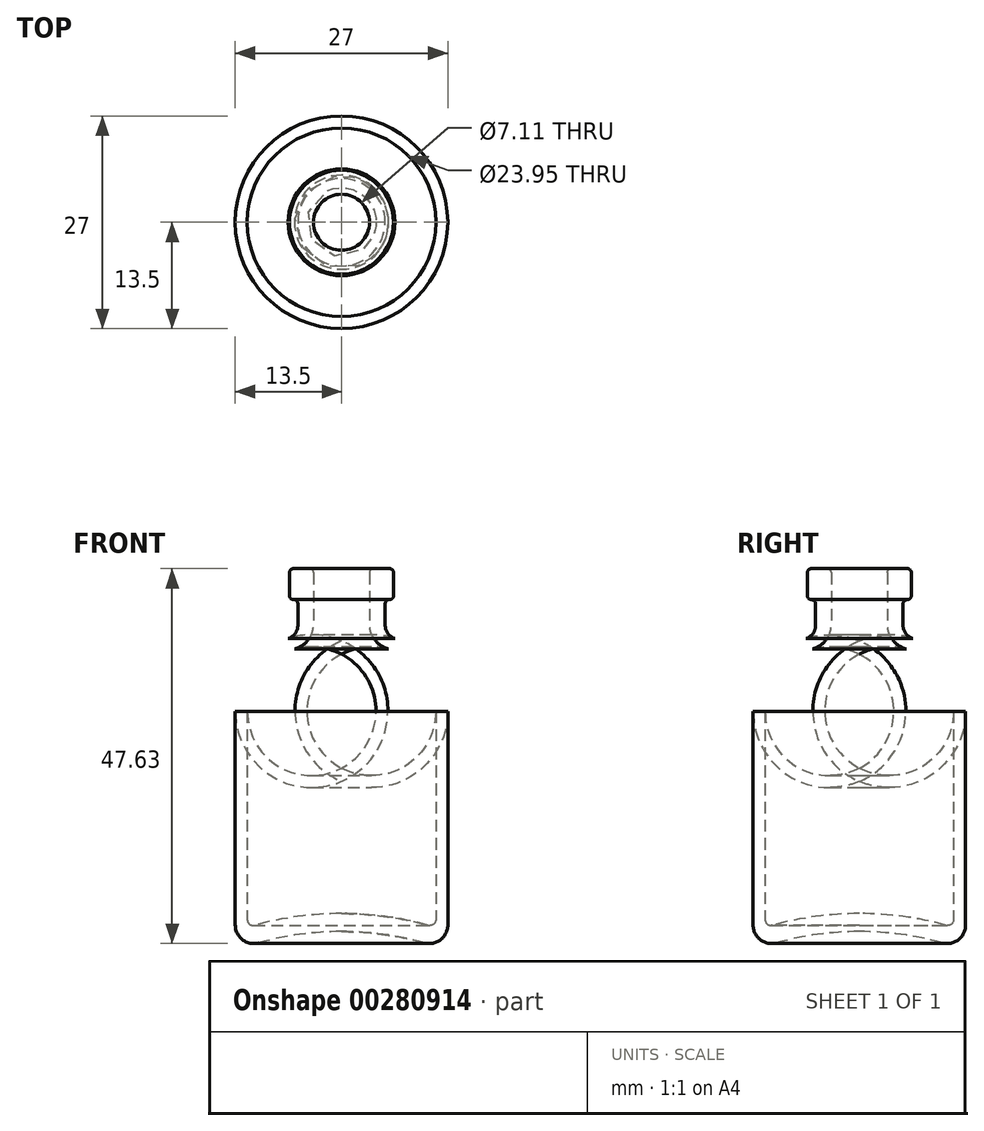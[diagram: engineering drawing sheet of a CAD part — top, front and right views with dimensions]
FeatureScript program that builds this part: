
annotation { "Feature Type Name" : "Feature", "Feature Type Description" : "" }
export const myFeature = defineFeature(function(context is Context, id is Id, definition is map)
    precondition{}
    {
        {
            var Q0;
            Q0=qCreatedBy(makeId("Front.planeOp"),FACE);
            var sketch = newSketch(context, id + "F0", { "sketchPlane" : qUnion([Q0])});
            skLineSegment(sketch, "E0", {"start": v(13.5, 29.51) * mm, "end": v(13.5, 2.36) * mm});
            skLineSegment(sketch, "E1", {"start": v(0, 0) * mm, "end": v(28.43, 0) * mm, "construction": true});
            skArc(sketch, "E2", {"start": v(10.5, 0.09) * mm, "mid": v(12.57, 0.48) * mm, "end": v(13.5, 2.36) * mm});
            skLineSegment(sketch, "E3", {"start": v(0.17, 1.52) * mm, "end": v(-0.17, 1.52) * mm, "construction": true});
            skLineSegment(sketch, "E4", {"start": v(0, 0) * mm, "end": v(0, 24.8) * mm, "construction": true});
            skPoint(sketch, "E4.endSnap0", {"position": v(0, 1.52) * mm});
            skArc(sketch, "E5", {"start": v(10.5, 0.09) * mm, "mid": v(5.3, 1.16) * mm, "end": v(0, 1.52) * mm});
            skArc(sketch, "E6", {"start": v(13.5, 29.51) * mm, "mid": v(11.64, 35.22) * mm, "end": v(6.78, 38.75) * mm});
            skLineSegment(sketch, "E7", {"start": v(5.55, 40.44) * mm, "end": v(5.55, 43.69) * mm});
            skLineSegment(sketch, "E8", {"start": v(5.55, 43.69) * mm, "end": v(6.6, 43.69) * mm});
            skLineSegment(sketch, "E9", {"start": v(6.6, 43.69) * mm, "end": v(6.6, 47.63) * mm});
            skLineSegment(sketch, "E10", {"start": v(6.6, 47.63) * mm, "end": v(3.56, 47.63) * mm});
            skLineSegment(sketch, "E11", {"start": v(3.56, 47.63) * mm, "end": v(3.56, 40.58) * mm});
            skPoint(sketch, "E12.newPointA", {"position": v(5.55, 40) * mm});
            skArc(sketch, "E12.filletArc", {"start": v(5.55, 40.44) * mm, "mid": v(5.9, 39.4) * mm, "end": v(6.78, 38.75) * mm});
            skArc(sketch, "E13", {"start": v(11.98, 29.51) * mm, "mid": v(10.3, 34.47) * mm, "end": v(5.98, 37.4) * mm});
            skArc(sketch, "E14", {"start": v(3.56, 40.58) * mm, "mid": v(4.23, 38.58) * mm, "end": v(5.98, 37.4) * mm});
            skArc(sketch, "E15.0", {"start": v(11.01, 2.32) * mm, "mid": v(5.56, 3.44) * mm, "end": v(0, 3.8) * mm});
            skLineSegment(sketch, "E16.0", {"start": v(11.98, 29.51) * mm, "end": v(11.98, 3.05) * mm});
            skArc(sketch, "E17.filletArc", {"start": v(11.01, 2.32) * mm, "mid": v(11.68, 2.45) * mm, "end": v(11.98, 3.05) * mm});
            skLineSegment(sketch, "E18", {"start": v(0, 3.81) * mm, "end": v(0, 1.52) * mm});
            skSolve(sketch);
        }
        {
            var Q0;
            Q0 = qSketchRegion(id + "F0", true);
            var Q1;
            Q1=sQuery(id+"F0.wireOp",EDGE,"E4");
            revolve(context, id + "F1", {"entities" : qUnion([Q0]), "axis" : qUnion([Q1]), "revolveType" : RevolveType.FULL});
        }
        {
            var Q0;
            Q0=makeQuery(id+"F1.opRevolve","SWEPT_EDGE",EDGE,{"disambiguationData":[OSD([sQuery(id+"F0.wireOp",EDGE,"E7"),sQuery(id+"F0.wireOp",EDGE,"E8")])]});
            var Q1;
            Q1=makeQuery(id+"F1.opRevolve","SWEPT_EDGE",EDGE,{"disambiguationData":[OSD([sQuery(id+"F0.wireOp",EDGE,"E8"),sQuery(id+"F0.wireOp",EDGE,"E9")])]});
            var Q2;
            Q2=makeQuery(id+"F1.opRevolve","SWEPT_EDGE",EDGE,{"disambiguationData":[OSD([sQuery(id+"F0.wireOp",EDGE,"E9"),sQuery(id+"F0.wireOp",EDGE,"E10")])]});
            var Q3;
            Q3=makeQuery(id+"F1.opRevolve","SWEPT_EDGE",EDGE,{"disambiguationData":[OSD([sQuery(id+"F0.wireOp",EDGE,"E10"),sQuery(id+"F0.wireOp",EDGE,"E11")])]});
            fillet(context, id + "F2", {"entities" : qUnion([Q0, Q1, Q2, Q3]), "radius" : 0.5 * mm, "tangentPropagation" : true, "allowEdgeOverflow" : false});
        }
    });
